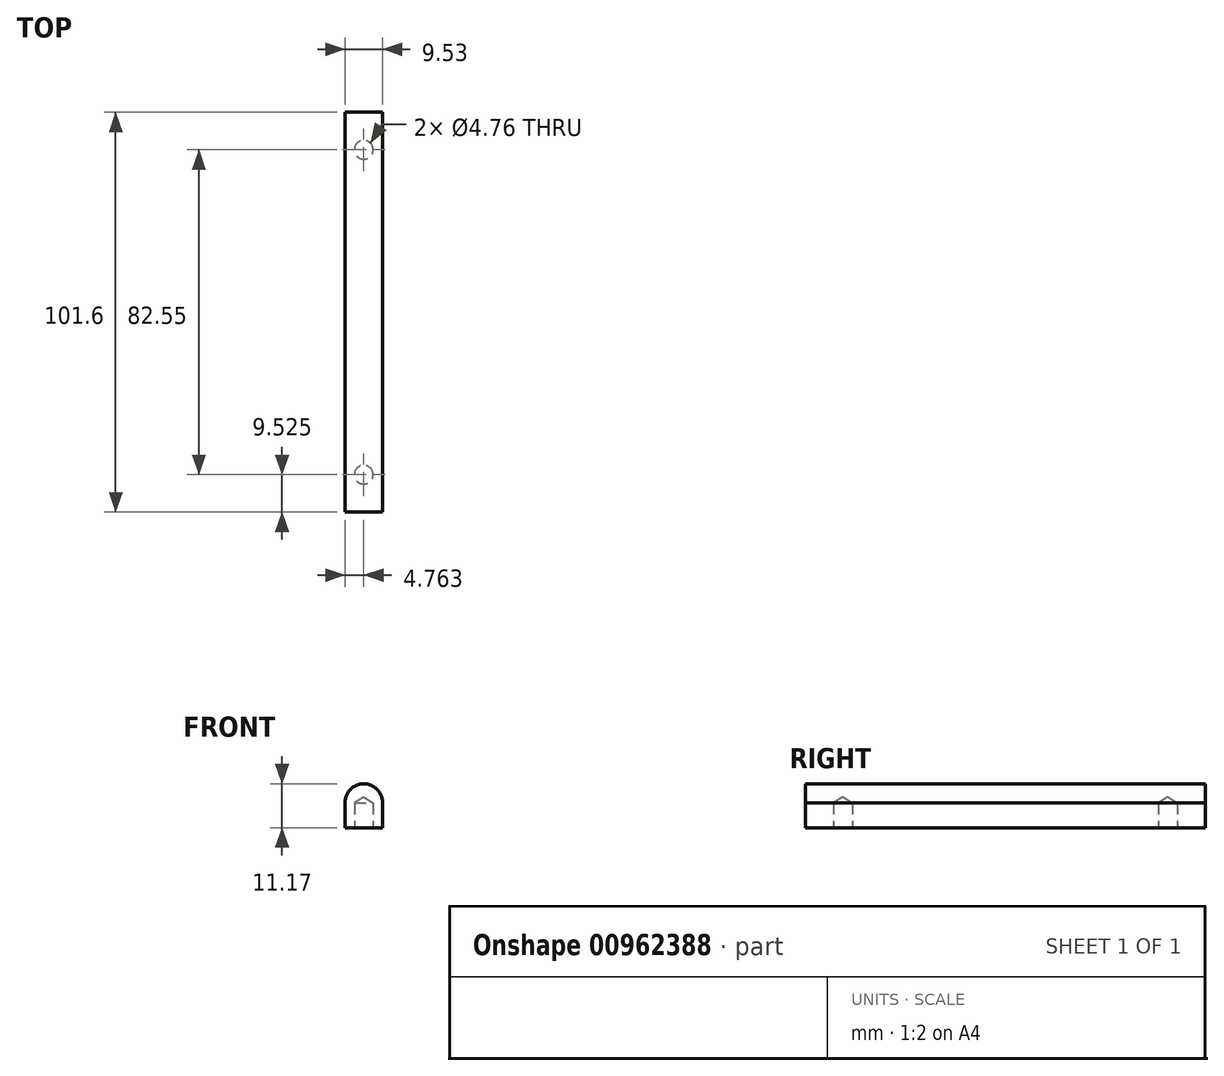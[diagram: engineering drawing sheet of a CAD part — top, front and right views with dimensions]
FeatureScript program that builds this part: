
annotation { "Feature Type Name" : "Feature", "Feature Type Description" : "" }
export const myFeature = defineFeature(function(context is Context, id is Id, definition is map)
    precondition{}
    {
        {
            var Q0;
            Q0=qCreatedBy(makeId("Front.planeOp"),FACE);
            var sketch = newSketch(context, id + "F0", { "sketchPlane" : qUnion([Q0])});
            skLineSegment(sketch, "E0.bottom", {"start": v(0, 0) * mm, "end": v(9.52, 0) * mm});
            skLineSegment(sketch, "E0.top", {"start": v(0, 6.35) * mm, "end": v(9.53, 6.35) * mm});
            skLineSegment(sketch, "E0.left", {"start": v(0, 0) * mm, "end": v(0, 6.35) * mm});
            skLineSegment(sketch, "E0.right", {"start": v(9.53, 0) * mm, "end": v(9.53, 6.35) * mm});
            skCircle(sketch, "E1", {"center": v(4.76, 6.41) * mm, "radius": 4.76 * mm});
            skSolve(sketch);
        }
        {
            var Q0;
            Q0 = qSketchRegion(id + "F0", true);
            extrude(context, id + "F1", {"entities" : qUnion([Q0]), "depth" : 101.6 * mm, "offsetDistance" : 25.4 * mm});
        }
        {
            var Q0;
            Q0=makeQuery(id+"F1.opExtrude","SWEPT_FACE",FACE,{"disambiguationData":[OSD([sQuery(id+"F0.wireOp",EDGE,"E0.bottom")])]});
            var sketch = newSketch(context, id + "F2", { "sketchPlane" : qUnion([Q0])});
            skCircle(sketch, "E2", {"center": v(4.76, 9.53) * mm, "radius": 2.38 * mm});
            skCircle(sketch, "E3", {"center": v(4.76, 92.08) * mm, "radius": 2.38 * mm});
            skSolve(sketch);
        }
        {
            var Q0;
            Q0=sQuery(id+"F2.wireOp",VERTEX,"E3.center");
            var Q1;
            Q1=sQuery(id+"F2.wireOp",VERTEX,"E2.center");
            var Q2;
            Q2=makeQuery(id+"F1.opExtrude","SWEPT_BODY",BODY,{"disambiguationData":[OSD([sQuery(id+"F0.wireOp",EDGE,"E0.bottom"),sQuery(id+"F0.wireOp",EDGE,"E0.top"),sQuery(id+"F0.wireOp",EDGE,"E0.left"),sQuery(id+"F0.wireOp",EDGE,"E0.right"),sQuery(id+"F0.wireOp",EDGE,"E1")])]});
            hole(context, id + "F3", {"style" : HoleStyle.SIMPLE, "endStyle" : HoleEndStyle.BLIND, "holeDiameter" : 4.76 * mm, "majorDiameter" : 6.35 * mm, "holeDepth" : 6.35 * mm, "isTappedThrough" : true, "tappedDepth" : 12.7 * mm, "tapClearance" : 3, "startFromSketch" : true, "locations" : qUnion([Q0, Q1]), "scope" : qUnion([Q2])});
        }
    });
